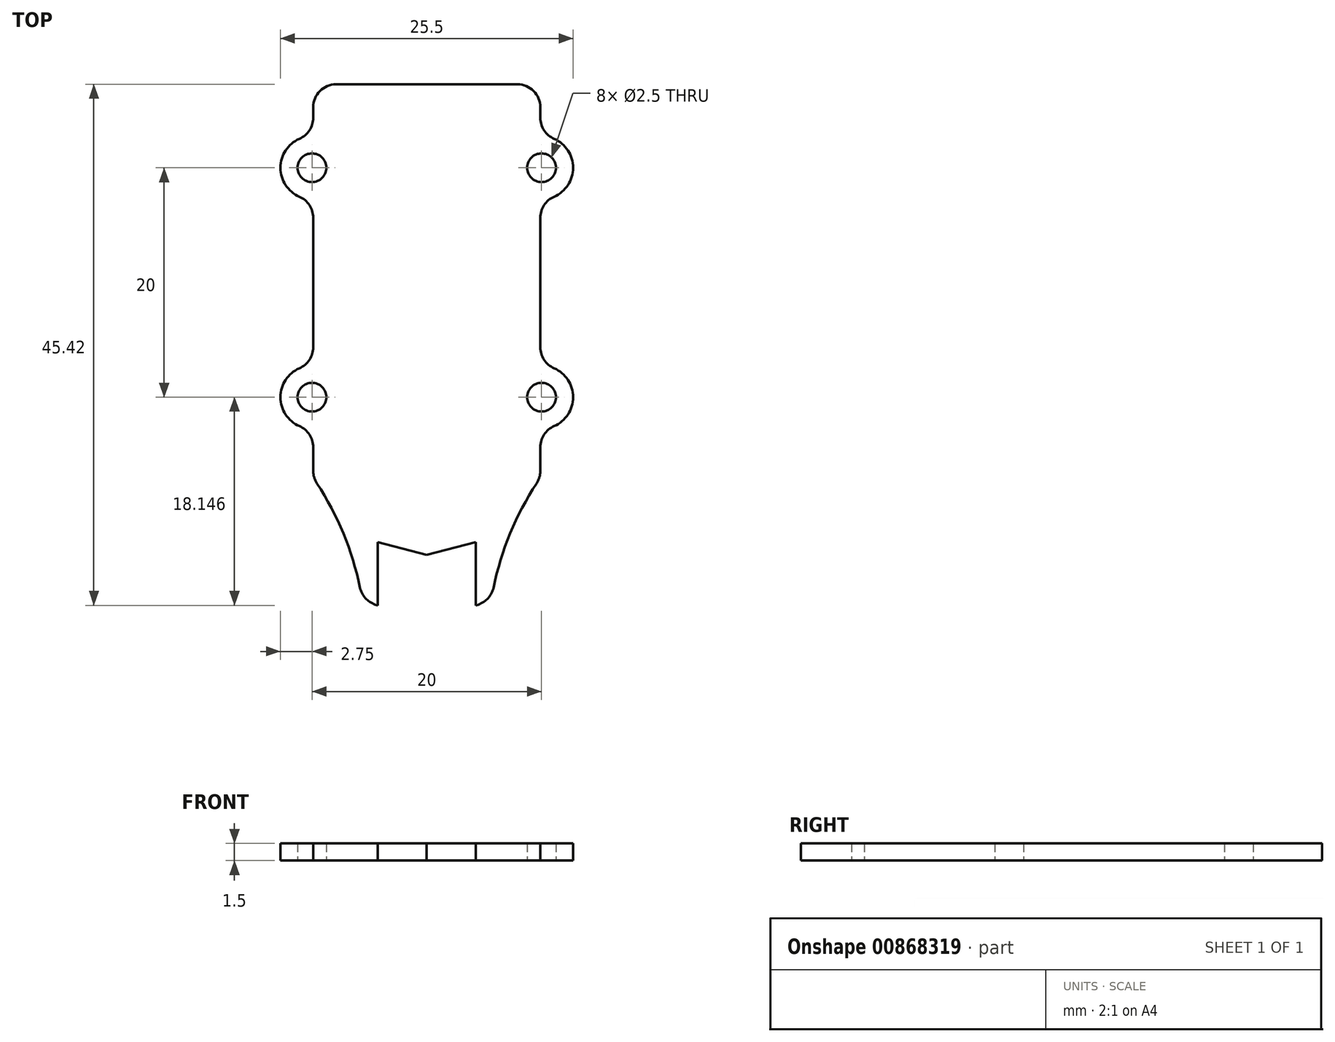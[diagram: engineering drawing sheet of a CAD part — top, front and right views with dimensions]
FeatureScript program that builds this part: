
annotation { "Feature Type Name" : "Feature", "Feature Type Description" : "" }
export const myFeature = defineFeature(function(context is Context, id is Id, definition is map)
    precondition{}
    {
        {
            var Q0;
            Q0=qCreatedBy(makeId("Top.planeOp"),FACE);
            var sketch = newSketch(context, id + "F0", { "sketchPlane" : qUnion([Q0])});
            skArc(sketch, "E0.MirrorC", {"start": v(5.81, -2.84) * mm, "mid": v(7.27, 1.87) * mm, "end": v(9.57, 6.24) * mm});
            skLineSegment(sketch, "E1", {"start": v(4.27, -4.4) * mm, "end": v(4.48, -4.33) * mm});
            skLineSegment(sketch, "E2", {"start": v(-4.27, 1.12) * mm, "end": v(0, 0) * mm});
            skLineSegment(sketch, "E3.MirrorCS", {"start": v(4.27, -4.4) * mm, "end": v(4.27, 1.12) * mm});
            skLineSegment(sketch, "E4.MirrorCS", {"start": v(4.27, 1.12) * mm, "end": v(0, 0) * mm});
            skPoint(sketch, "E5.orphan", {"position": v(-4.27, -4.4) * mm});
            skPoint(sketch, "E6.visualSharp", {"position": v(-4.27, -4.2) * mm});
            skLineSegment(sketch, "E7.left", {"start": v(-9.9, 7.33) * mm, "end": v(-9.9, 9.39) * mm});
            skLineSegment(sketch, "E8.MirrorCS", {"start": v(9.9, 7.33) * mm, "end": v(9.9, 9.39) * mm});
            skLineSegment(sketch, "E9", {"start": v(-7.9, 41.02) * mm, "end": v(7.9, 41.02) * mm});
            skArc(sketch, "E10.0", {"start": v(-11.1, 36.27) * mm, "mid": v(-12.75, 33.75) * mm, "end": v(-11.1, 31.22) * mm});
            skArc(sketch, "E11.0", {"start": v(-11.1, 16.27) * mm, "mid": v(-12.75, 13.75) * mm, "end": v(-11.1, 11.22) * mm});
            skArc(sketch, "E12.MirrorC", {"start": v(11.1, 36.27) * mm, "mid": v(12.75, 33.75) * mm, "end": v(11.1, 31.22) * mm});
            skArc(sketch, "E13.MirrorC", {"start": v(11.1, 16.27) * mm, "mid": v(12.75, 13.75) * mm, "end": v(11.1, 11.22) * mm});
            skLineSegment(sketch, "E14.trimOffspring", {"start": v(-9.9, 18.1) * mm, "end": v(-9.9, 29.39) * mm});
            skLineSegment(sketch, "E15.trimOffspring", {"start": v(-9.9, 38.1) * mm, "end": v(-9.9, 39.02) * mm});
            skLineSegment(sketch, "E16.trimOffspring", {"start": v(9.9, 38.1) * mm, "end": v(9.9, 39.02) * mm});
            skLineSegment(sketch, "E17.trimOffspring", {"start": v(9.9, 18.1) * mm, "end": v(9.9, 29.39) * mm});
            skPoint(sketch, "E18.visualSharp", {"position": v(-9.9, 31) * mm});
            skArc(sketch, "E18.filletArc", {"start": v(-9.9, 29.39) * mm, "mid": v(-10.22, 30.49) * mm, "end": v(-11.1, 31.22) * mm});
            skPoint(sketch, "E19.visualSharp", {"position": v(-9.9, 16.5) * mm});
            skArc(sketch, "E19.filletArc", {"start": v(-11.1, 16.27) * mm, "mid": v(-10.22, 17) * mm, "end": v(-9.9, 18.1) * mm});
            skPoint(sketch, "E20.visualSharp", {"position": v(9.9, 16.5) * mm});
            skArc(sketch, "E20.filletArc", {"start": v(9.9, 18.1) * mm, "mid": v(10.22, 17) * mm, "end": v(11.1, 16.27) * mm});
            skPoint(sketch, "E21.visualSharp", {"position": v(9.9, 31) * mm});
            skArc(sketch, "E21.filletArc", {"start": v(11.1, 31.22) * mm, "mid": v(10.22, 30.49) * mm, "end": v(9.9, 29.39) * mm});
            skPoint(sketch, "E22.visualSharp", {"position": v(-9.9, 36.5) * mm});
            skArc(sketch, "E22.filletArc", {"start": v(-11.1, 36.27) * mm, "mid": v(-10.22, 37) * mm, "end": v(-9.9, 38.1) * mm});
            skPoint(sketch, "E23.visualSharp", {"position": v(9.9, 36.5) * mm});
            skArc(sketch, "E23.filletArc", {"start": v(9.9, 38.1) * mm, "mid": v(10.22, 37) * mm, "end": v(11.1, 36.27) * mm});
            skPoint(sketch, "E24.visualSharp", {"position": v(-9.9, 11) * mm});
            skArc(sketch, "E24.filletArc", {"start": v(-9.9, 9.39) * mm, "mid": v(-10.22, 10.49) * mm, "end": v(-11.1, 11.22) * mm});
            skPoint(sketch, "E25.visualSharp", {"position": v(9.9, 11) * mm});
            skArc(sketch, "E25.filletArc", {"start": v(11.1, 11.22) * mm, "mid": v(10.22, 10.49) * mm, "end": v(9.9, 9.39) * mm});
            skPoint(sketch, "E26.visualSharp", {"position": v(-9.9, 6.72) * mm});
            skArc(sketch, "E26.filletArc", {"start": v(-9.9, 7.33) * mm, "mid": v(-9.81, 6.76) * mm, "end": v(-9.57, 6.24) * mm});
            skPoint(sketch, "E27.visualSharp", {"position": v(-9.9, 41.02) * mm});
            skArc(sketch, "E27.filletArc", {"start": v(-7.9, 41.02) * mm, "mid": v(-9.3, 40.43) * mm, "end": v(-9.9, 39.02) * mm});
            skPoint(sketch, "E28.visualSharp", {"position": v(9.9, 41.02) * mm});
            skArc(sketch, "E28.filletArc", {"start": v(9.9, 39.02) * mm, "mid": v(9.3, 40.43) * mm, "end": v(7.9, 41.02) * mm});
            skPoint(sketch, "E29.visualSharp", {"position": v(9.9, 6.72) * mm});
            skArc(sketch, "E29.filletArc", {"start": v(9.57, 6.24) * mm, "mid": v(9.81, 6.76) * mm, "end": v(9.9, 7.33) * mm});
            skPoint(sketch, "E30.visualSharp", {"position": v(5.6, -3.96) * mm});
            skArc(sketch, "E30.filletArc", {"start": v(4.48, -4.33) * mm, "mid": v(5.35, -3.77) * mm, "end": v(5.81, -2.84) * mm});
            skArc(sketch, "E31.MirrorCS", {"start": v(-4.48, -4.33) * mm, "mid": v(-5.35, -3.77) * mm, "end": v(-5.81, -2.84) * mm});
            skLineSegment(sketch, "E32.MirrorCS", {"start": v(-4.27, -4.4) * mm, "end": v(-4.48, -4.33) * mm});
            skPoint(sketch, "E33.MirrorCS.end.orphan", {"position": v(-9.57, 6.24) * mm});
            skPoint(sketch, "E33.MirrorCS.start.orphan", {"position": v(-5.81, -2.84) * mm});
            skArc(sketch, "E34.MirrorCS", {"start": v(-5.81, -2.84) * mm, "mid": v(-7.27, 1.87) * mm, "end": v(-9.57, 6.24) * mm});
            skLineSegment(sketch, "E35.MirrorCS", {"start": v(-4.27, -4.4) * mm, "end": v(-4.27, 1.12) * mm});
            skCircle(sketch, "E36", {"center": v(-10, 13.75) * mm, "radius": 1.25 * mm});
            skCircle(sketch, "E37", {"center": v(-10, 33.75) * mm, "radius": 1.25 * mm});
            skCircle(sketch, "E38", {"center": v(10, 33.75) * mm, "radius": 1.25 * mm});
            skCircle(sketch, "E39", {"center": v(10, 13.75) * mm, "radius": 1.25 * mm});
            skSolve(sketch);
        }
        {
            var Q0;
            Q0 = qSketchRegion(id + "F0", true);
            extrude(context, id + "F1", {"entities" : qUnion([Q0]), "depth" : 1.5 * mm, "offsetDistance" : 25 * mm});
        }
    });
